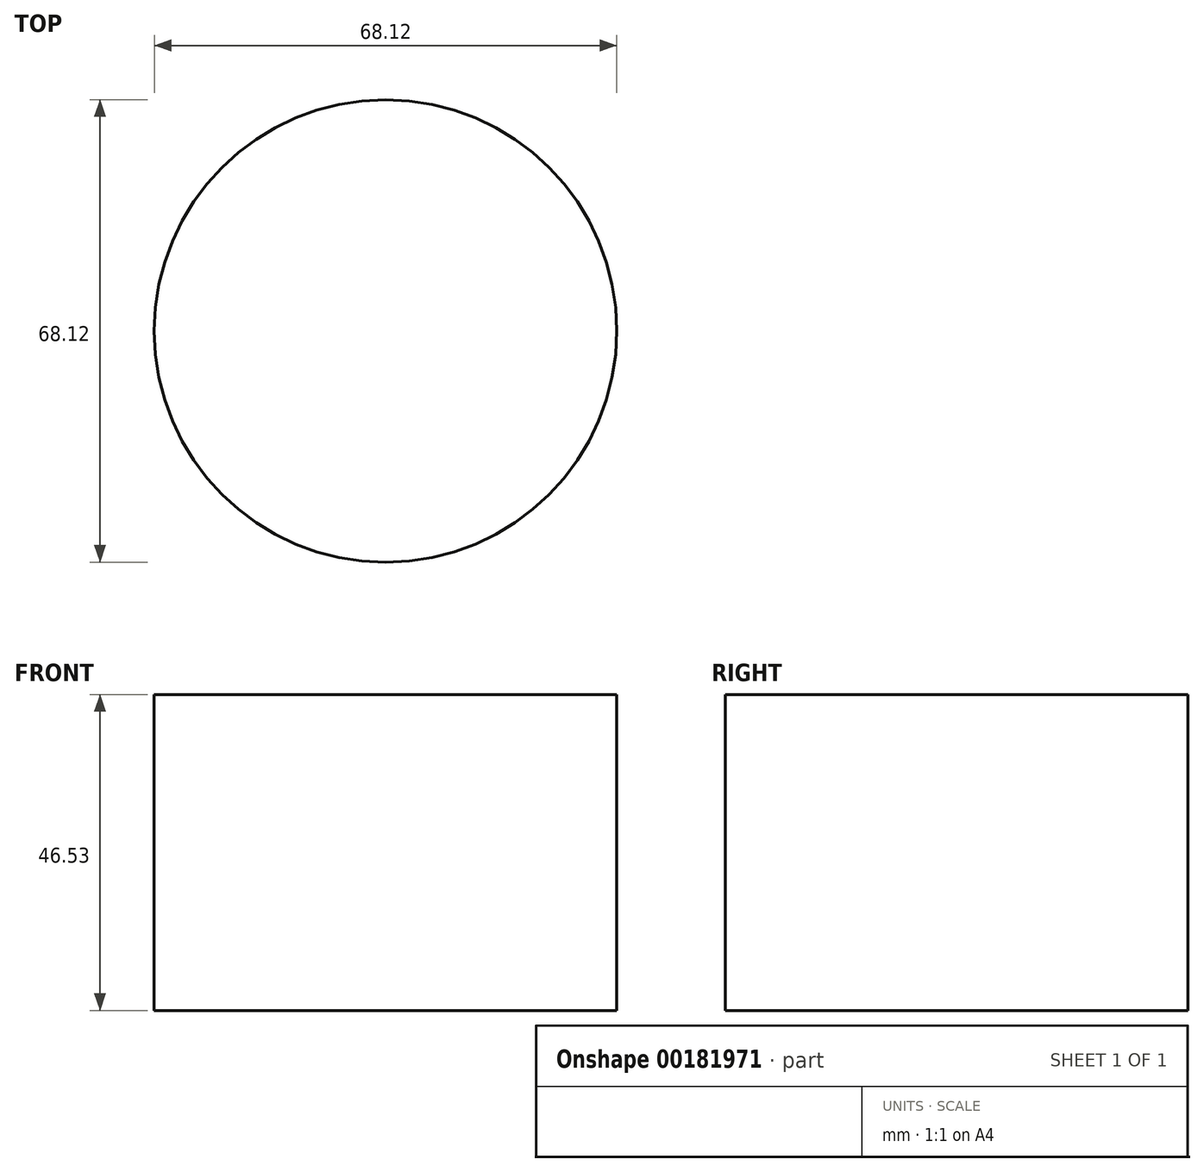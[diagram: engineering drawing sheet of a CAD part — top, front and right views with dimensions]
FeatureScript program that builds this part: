
annotation { "Feature Type Name" : "Feature", "Feature Type Description" : "" }
export const myFeature = defineFeature(function(context is Context, id is Id, definition is map)
    precondition{}
    {
        {
            var Q0;
            Q0=qCreatedBy(makeId("Top.planeOp"),FACE);
            var sketch = newSketch(context, id + "F0", { "sketchPlane" : qUnion([Q0])});
            skCircle(sketch, "E0", {"center": v(0, 0) * mm, "radius": 34.06 * mm});
            skSolve(sketch);
        }
        {
            var Q0;
            Q0=makeQuery(id+"F0.imprint","IMPRINT",FACE,{"disambiguationData":[TD([[makeQuery(id+"F0.imprint","IMPRINT",EDGE,{"derivedFrom":sQuery(id+"F0.wireOp",EDGE,"E0")}),1.0]])]});
            extrude(context, id + "F1", {"entities" : qUnion([Q0]), "depth" : 46.53 * mm});
        }
    });
